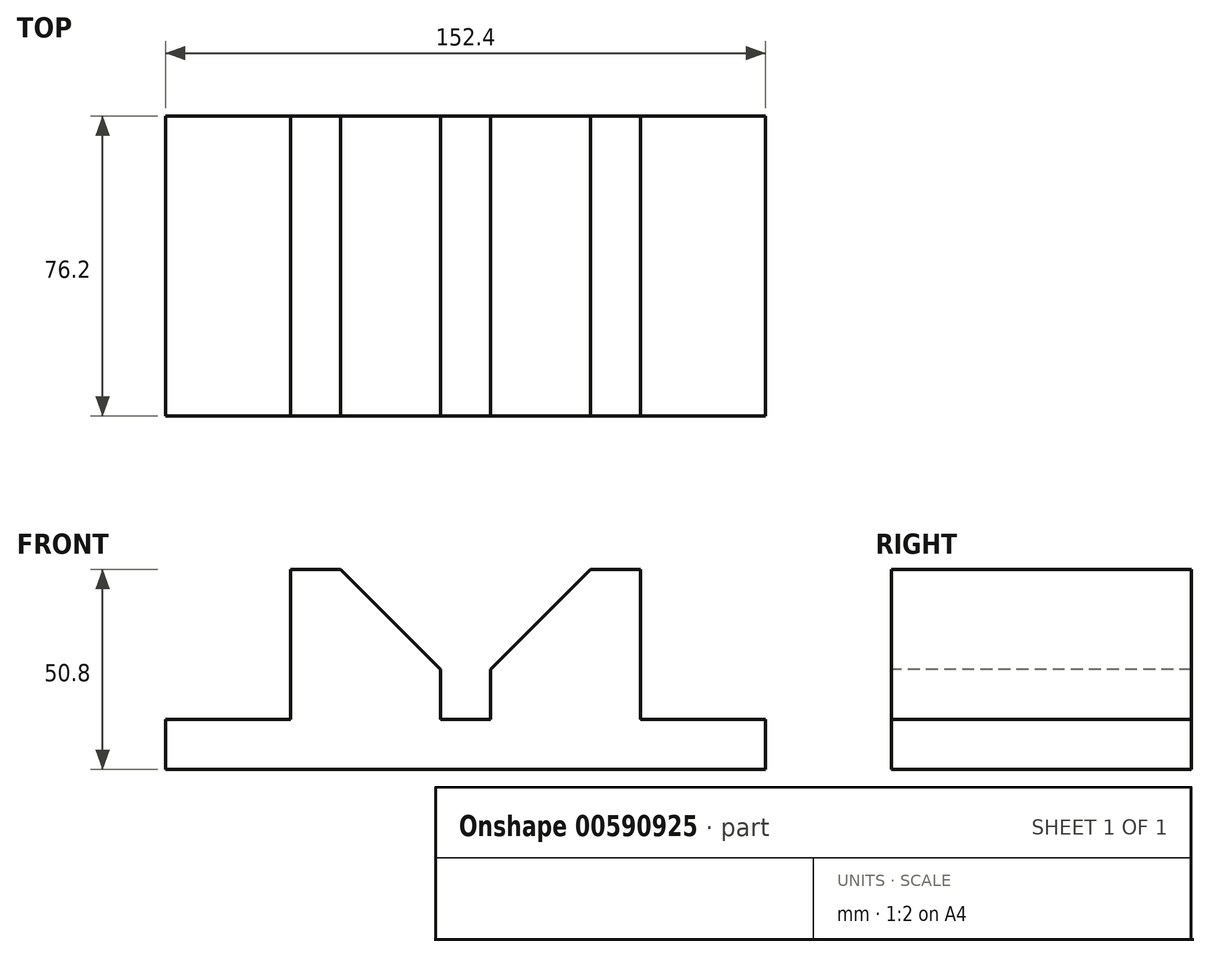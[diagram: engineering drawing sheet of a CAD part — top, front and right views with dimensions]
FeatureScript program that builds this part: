
annotation { "Feature Type Name" : "Feature", "Feature Type Description" : "" }
export const myFeature = defineFeature(function(context is Context, id is Id, definition is map)
    precondition{}
    {
        {
            var Q0;
            Q0=qCreatedBy(makeId("Front.planeOp"),FACE);
            var sketch = newSketch(context, id + "F0", { "sketchPlane" : qUnion([Q0])});
            skLineSegment(sketch, "E0", {"start": v(0, 0) * mm, "end": v(152.4, 0) * mm});
            skLineSegment(sketch, "E1", {"start": v(0, 0) * mm, "end": v(0, 12.7) * mm});
            skLineSegment(sketch, "E2", {"start": v(0, 12.7) * mm, "end": v(31.75, 12.7) * mm});
            skLineSegment(sketch, "E3", {"start": v(31.75, 12.7) * mm, "end": v(31.75, 50.8) * mm});
            skLineSegment(sketch, "E4", {"start": v(31.75, 50.8) * mm, "end": v(44.45, 50.8) * mm});
            skLineSegment(sketch, "E5", {"start": v(152.4, 0) * mm, "end": v(152.4, 12.7) * mm});
            skLineSegment(sketch, "E6", {"start": v(152.4, 12.7) * mm, "end": v(120.65, 12.7) * mm});
            skLineSegment(sketch, "E7", {"start": v(120.65, 12.7) * mm, "end": v(120.65, 50.8) * mm});
            skLineSegment(sketch, "E8", {"start": v(120.65, 50.8) * mm, "end": v(107.95, 50.8) * mm});
            skPoint(sketch, "E9", {"position": v(69.85, 12.7) * mm});
            skLineSegment(sketch, "E10", {"start": v(69.85, 12.7) * mm, "end": v(82.55, 12.7) * mm});
            skLineSegment(sketch, "E11", {"start": v(82.55, 12.7) * mm, "end": v(69.85, 12.7) * mm});
            skLineSegment(sketch, "E12", {"start": v(69.85, 25.4) * mm, "end": v(69.85, 12.7) * mm});
            skLineSegment(sketch, "E13", {"start": v(82.55, 12.7) * mm, "end": v(82.55, 25.4) * mm});
            skLineSegment(sketch, "E14", {"start": v(44.45, 50.8) * mm, "end": v(69.85, 25.4) * mm});
            skLineSegment(sketch, "E15", {"start": v(82.55, 25.4) * mm, "end": v(107.95, 50.8) * mm});
            skSolve(sketch);
        }
        {
            var Q0;
            Q0=makeQuery(id+"F0.imprint","IMPRINT",FACE,{"disambiguationData":[TD([[makeQuery(id+"F0.imprint","IMPRINT",EDGE,{"derivedFrom":sQuery(id+"F0.wireOp",EDGE,"E0")}),1.0]])]});
            extrude(context, id + "F1", {"entities" : qUnion([Q0]), "oppositeDirection" : true, "depth" : 76.2 * mm, "offsetDistance" : 25.4 * mm});
        }
    });
